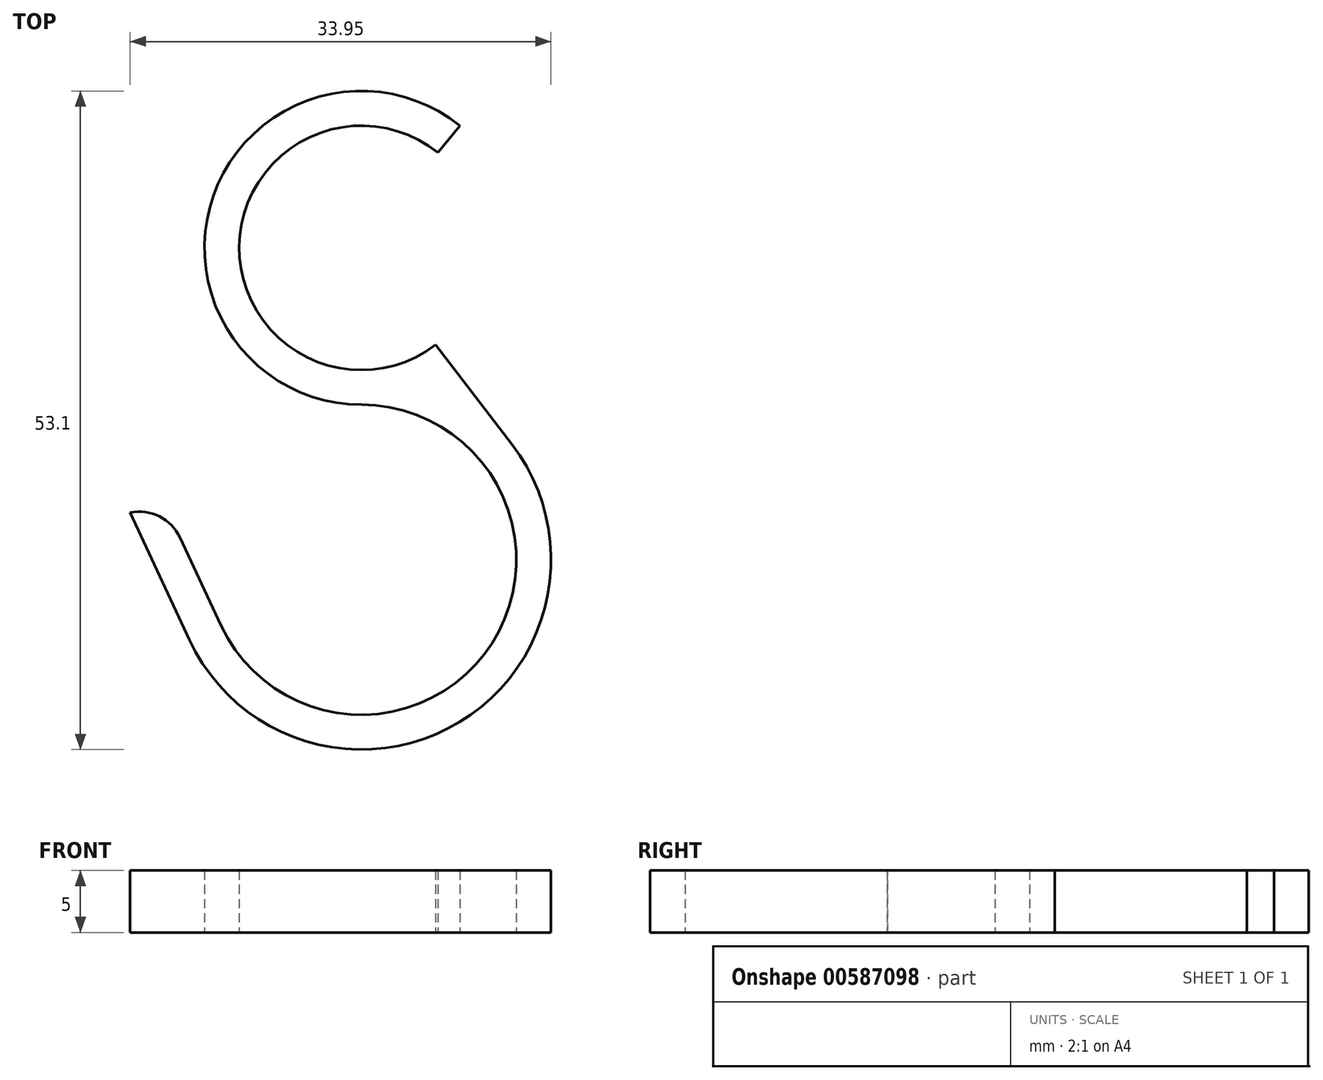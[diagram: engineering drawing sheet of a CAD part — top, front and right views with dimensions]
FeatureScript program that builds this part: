
annotation { "Feature Type Name" : "Feature", "Feature Type Description" : "" }
export const myFeature = defineFeature(function(context is Context, id is Id, definition is map)
    precondition{}
    {
        {
            var Q0;
            Q0=qCreatedBy(makeId("Top.planeOp"),FACE);
            var sketch = newSketch(context, id + "F0", { "sketchPlane" : qUnion([Q0])});
            skCircle(sketch, "E0", {"center": v(0, 0) * mm, "radius": 9.85 * mm});
            skCircle(sketch, "E1", {"center": v(0, -25.15) * mm, "radius": 12.5 * mm});
            skArc(sketch, "E2", {"start": v(7.94, 9.85) * mm, "mid": v(-11.93, 4.2) * mm, "end": v(0, -12.65) * mm});
            skLineSegment(sketch, "E3", {"start": v(7.55, -9.85) * mm, "end": v(6, -7.82) * mm});
            skLineSegment(sketch, "E4", {"start": v(7.94, 9.85) * mm, "end": v(6.18, 7.67) * mm});
            skLineSegment(sketch, "E5", {"start": v(7.94, 9.85) * mm, "end": v(0, 9.85) * mm, "construction": true});
            skLineSegment(sketch, "E6", {"start": v(6.18, 7.67) * mm, "end": v(0, 0) * mm, "construction": true});
            skLineSegment(sketch, "E7", {"start": v(0, 0) * mm, "end": v(6, -7.82) * mm, "construction": true});
            skLineSegment(sketch, "E8", {"start": v(7.55, -9.85) * mm, "end": v(0, -9.85) * mm, "construction": true});
            skLineSegment(sketch, "E9", {"start": v(-13.87, -31.62) * mm, "end": v(-18.65, -21.35) * mm});
            skLineSegment(sketch, "E10", {"start": v(-18.65, -21.35) * mm, "end": v(-16.12, -20.17) * mm});
            skLineSegment(sketch, "E11", {"start": v(-16.12, -20.17) * mm, "end": v(-11.33, -30.43) * mm});
            skArc(sketch, "E12", {"start": v(-13.87, -31.62) * mm, "mid": v(7.93, -38.23) * mm, "end": v(12.14, -15.84) * mm});
            skLineSegment(sketch, "E13", {"start": v(-12.5, -25.15) * mm, "end": v(12.5, -25.15) * mm, "construction": true});
            skLineSegment(sketch, "E14", {"start": v(0, -25.15) * mm, "end": v(-13.87, -31.62) * mm, "construction": true});
            skLineSegment(sketch, "E15", {"start": v(-16.12, -20.17) * mm, "end": v(0, -12.65) * mm, "construction": true});
            skLineSegment(sketch, "E16", {"start": v(7.55, -9.85) * mm, "end": v(12.14, -15.84) * mm});
            skPoint(sketch, "E17.start.orphan", {"position": v(0, -12.65) * mm});
            skSolve(sketch);
        }
        {
            var Q0;
            {var subQ2=sQuery(id+"F0.wireOp",EDGE,"E2");Q0=makeQuery(id+"F0.imprint","IMPRINT",FACE,{"disambiguationData":[TD([[makeQuery(id+"F0.imprint","IMPRINT",EDGE,{"derivedFrom":subQ2}),1.0]])]});}
            var Q1;
            {var subQ0=sQuery(id+"F0.wireOp",EDGE,"E3");Q1=makeQuery(id+"F0.imprint","IMPRINT",FACE,{"disambiguationData":[TD([[makeQuery(id+"F0.imprint","IMPRINT",EDGE,{"derivedFrom":subQ0}),1.0]])]});}
            var Q2;
            {var subQ0=sQuery(id+"F0.wireOp",EDGE,"E9");Q2=makeQuery(id+"F0.imprint","IMPRINT",FACE,{"disambiguationData":[TD([[makeQuery(id+"F0.imprint","IMPRINT",EDGE,{"derivedFrom":subQ0}),-1.0]])]});}
            extrude(context, id + "F1", {"entities" : qUnion([Q0, Q1, Q2]), "depth" : 5 * mm, "offsetDistance" : 25 * mm});
        }
        {
            var Q0;
            Q0=makeQuery(id+"F1.opExtrude","SWEPT_EDGE",EDGE,{"disambiguationData":[OSD([sQuery(id+"F0.wireOp",EDGE,"E10"),sQuery(id+"F0.wireOp",EDGE,"E11")])]});
            fillet(context, id + "F2", {"entities" : qUnion([Q0]), "radius" : 3.62 * mm, "tangentPropagation" : true, "allowEdgeOverflow" : false});
        }
    });
